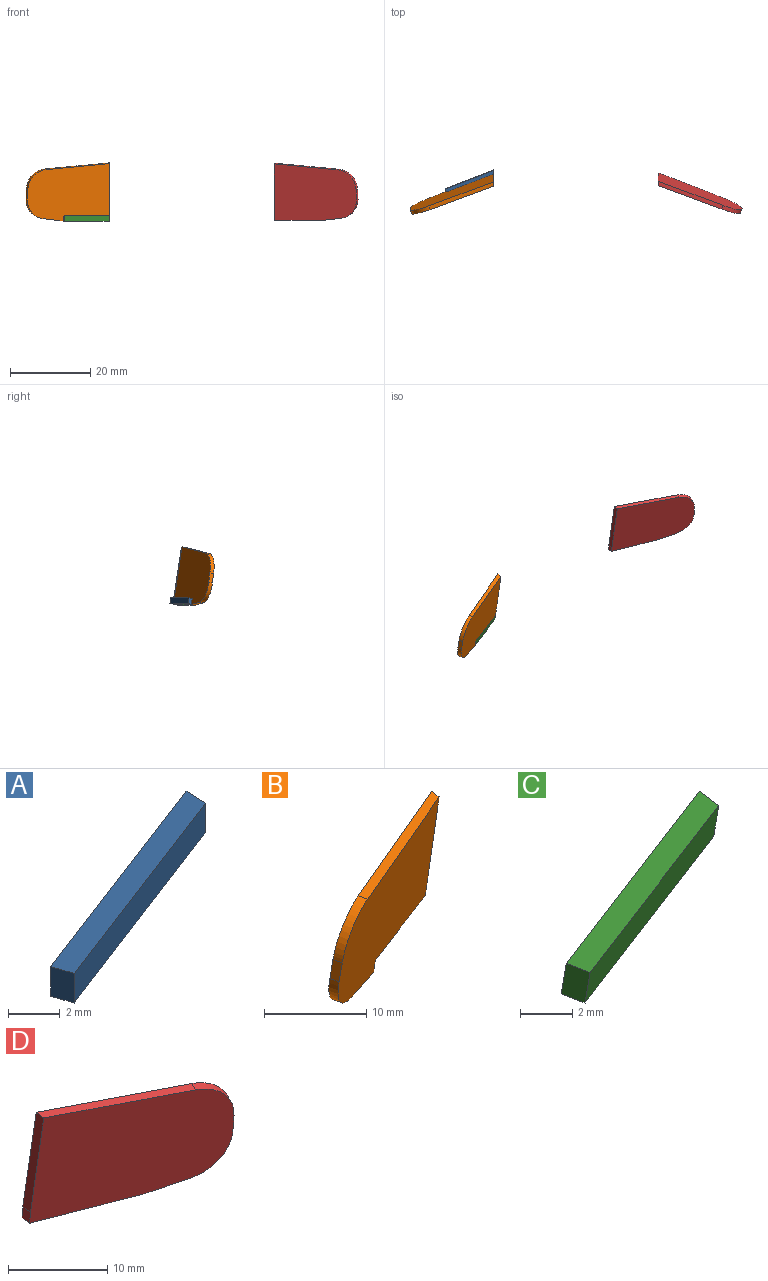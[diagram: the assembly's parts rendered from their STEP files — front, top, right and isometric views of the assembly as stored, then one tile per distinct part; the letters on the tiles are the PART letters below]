
ASSEMBLY  parts=4 mates=1
PART A: 6 faces, bbox 12x5.5x1.4 mm
  f0: plane 12x4.61mm, normal (-0.36,0.93,0), area 18mm2, adj f1,f3,f4,f5
  f1: plane 1.44x1.08mm, normal (1,-0.01,0), area 1.5mm2, adj f0,f2,f4,f5
  f2: plane 11.63x4.46mm, normal (0.36,-0.93,0), area 17.4mm2, adj f1,f3,f4,f5
  f3: plane 1.44x0.93mm, normal (-0.93,-0.36,0), area 1.4mm2, adj f0,f2,f4,f5
  f4: plane 12x5.54mm, normal (-0.01,0.03,-1), area 12.7mm2, adj f0,f1,f2,f3
  f5: plane 12x5.54mm, normal (0.01,-0.03,1), area 12.7mm2, adj f0,f1,f2,f3
PART B: 10 faces, bbox 20.7x9.9x14.5 mm
  f0: plane 11.63x5.39mm, normal (-0.05,0.13,-0.99), area 12.3mm2, adj f6,f7,f8,f9
  f1: plane 16.11x6.88mm, normal (-0.03,-0.16,0.99), area 17mm2, adj f2,f7,f8,f9
  f2: extruded ~5.07x4.85mm, area 7.4mm2, adj f1,f3,f7,f8
  f3: plane 2.47x1.23mm, normal (-0.93,-0.36,0), area 2.4mm2, adj f2,f4,f7,f8
  f4: extruded ~5.09x4.28mm, area 7.3mm2, adj f3,f5,f7,f8
  f5: plane 5.54x3mm, normal (-0.15,0.09,-0.98), area 5.6mm2, adj f4,f6,f7,f8
  f6: plane 1.64x1.15mm, normal (0.93,0.35,0.05), area 1.5mm2, adj f0,f5,f7,f8
  f7: plane 20.36x14.29mm, normal (0.35,-0.92,-0.14), area 260.8mm2, adj f0,f1,f2,f3,f4,f5,f6,f9
  f8: plane 20.74x14.33mm, normal (-0.35,0.92,0.14), area 266mm2, adj f0,f1,f2,f3,f4,f5,f6,f9
  f9: plane 12.97x2.99mm, normal (1,-0.02,0), area 14mm2, adj f0,f1,f7,f8
PART C: 6 faces, bbox 11.7x5.6x1.6 mm
  f0: plane 11.7x4.66mm, normal (-0.35,0.92,0.14), area 18.7mm2, adj f2,f3,f4,f5
  f1: plane 11.33x4.51mm, normal (0.35,-0.92,-0.14), area 18.1mm2, adj f2,f3,f4,f5
  f2: plane 1.62x1.12mm, normal (-0.93,-0.36,0), area 1.5mm2, adj f0,f1,f3,f4
  f3: plane 11.63x5.39mm, normal (-0.05,0.13,-0.99), area 12.3mm2, adj f0,f1,f2,f5
  f4: plane 11.63x5.39mm, normal (0.05,-0.13,0.99), area 12.3mm2, adj f0,f1,f2,f5
  f5: plane 1.62x1.26mm, normal (1,-0.01,-0.05), area 1.6mm2, adj f0,f1,f3,f4
PART D: 11 faces, bbox 20.8x10.1x14.3 mm
  f0: plane 5.2x2.87mm, normal (0.15,0.09,-0.98), area 5.2mm2, adj f1,f5,f6,f7
  f1: extruded ~5.09x4.28mm, area 7.3mm2, adj f0,f2,f6,f7
  f2: plane 2.3x1.21mm, normal (0.93,-0.36,0), area 2.2mm2, adj f1,f3,f6,f7
  f3: extruded ~5.07x4.85mm, area 7.4mm2, adj f2,f4,f6,f7
  f4: plane 16.15x6.91mm, normal (0.03,-0.16,0.99), area 17.1mm2, adj f3,f6,f7,f9
  f5: plane 0.93x0.36mm, normal (-0.93,0.35,0.05), area 0mm2, adj f0,f6,f7,f8
  f6: plane 20.39x14.09mm, normal (-0.36,-0.92,-0.14), area 275.3mm2, adj f0,f1,f2,f3,f4,f5,f8,f9
  f7: plane 20.76x14.13mm, normal (0.36,0.92,0.14), area 281mm2, adj f0,f1,f2,f3,f4,f5,f8,f9
  f8: plane 11.93x5.52mm, normal (0.05,0.13,-0.99), area 12.6mm2, adj f5,f6,f7,f10
  f9: plane 12.78x2.96mm, normal (-1,-0.02,0), area 13.7mm2, adj f4,f6,f7,f10
  f10: plane 1.62x1.26mm, normal (-1,-0.01,-0.05), area 1.6mm2, adj f6,f7,f8,f9
PLACE A rot(axis=(0.93,0.36,0.03),5deg) t=(-0.07,-17.79,-22.98)mm
PLACE B t=(0.02,-18.52,-24.59)mm
PLACE C t=(0.02,-18.52,-24.59)mm
PLACE D t=(0.02,-18.52,-24.59)mm
MATE fastened C.f4 <-> B.f0  axis (0.05,-0.13,0.99) through (-26.23,-49.01,-23.3)mm
